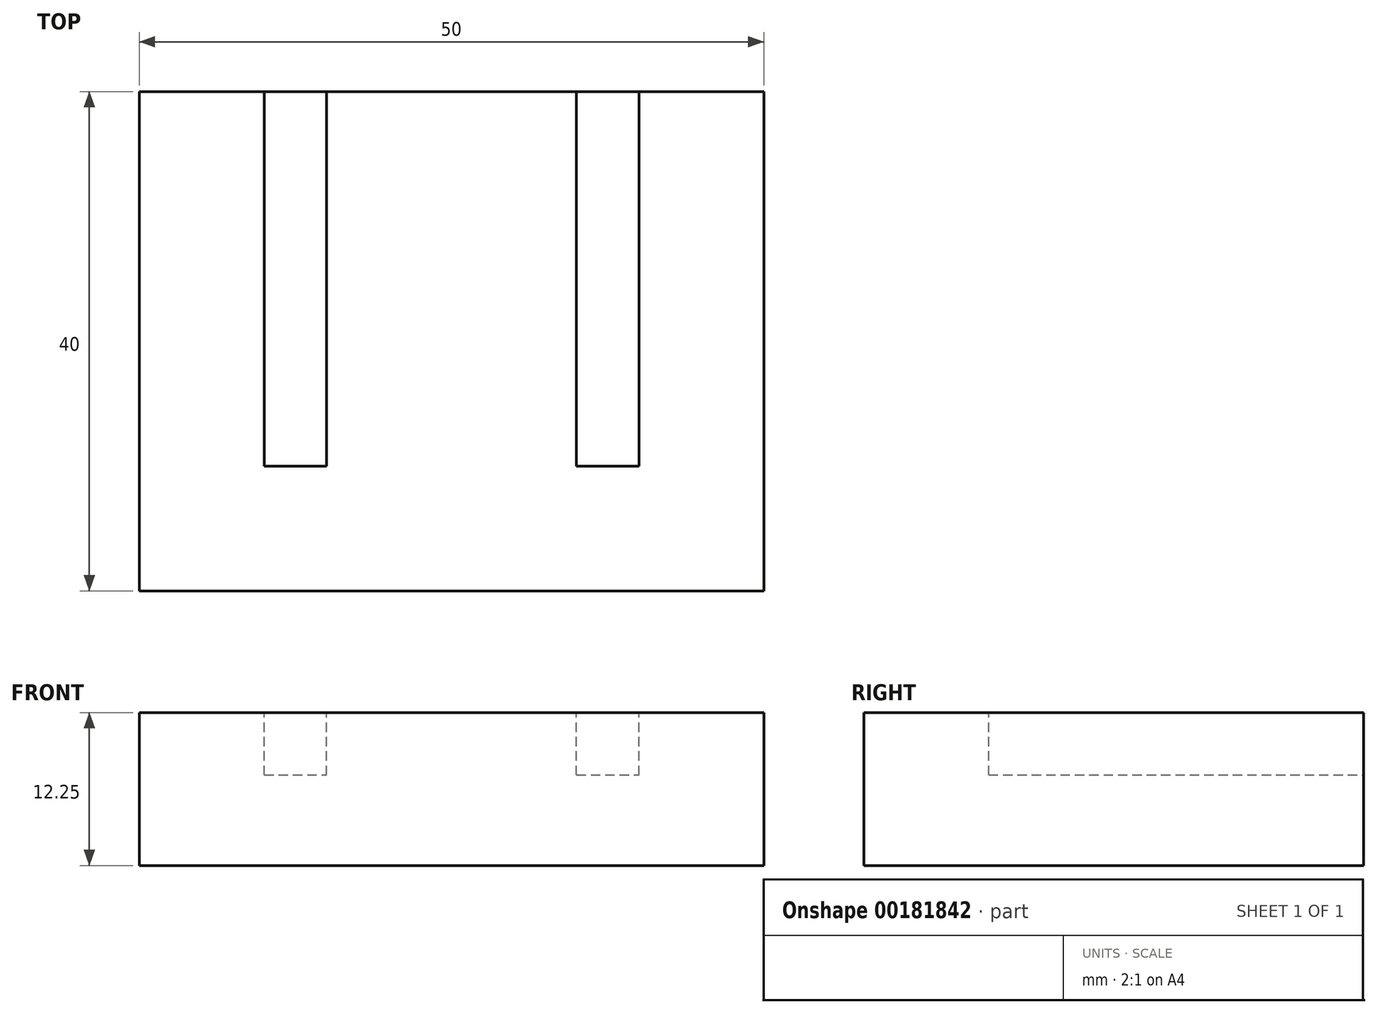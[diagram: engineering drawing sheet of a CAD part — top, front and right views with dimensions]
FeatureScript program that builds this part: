
annotation { "Feature Type Name" : "Feature", "Feature Type Description" : "" }
export const myFeature = defineFeature(function(context is Context, id is Id, definition is map)
    precondition{}
    {
        {
            var Q0;
            Q0=qCreatedBy(makeId("Top.planeOp"),FACE);
            var sketch = newSketch(context, id + "F0", { "sketchPlane" : qUnion([Q0])});
            skLineSegment(sketch, "E0.bottom", {"start": v(-26.25, 21.05) * mm, "end": v(23.75, 21.05) * mm});
            skLineSegment(sketch, "E0.top", {"start": v(-26.25, -18.95) * mm, "end": v(23.75, -18.95) * mm});
            skLineSegment(sketch, "E0.left", {"start": v(-26.25, 21.05) * mm, "end": v(-26.25, -18.95) * mm});
            skLineSegment(sketch, "E0.right", {"start": v(23.75, 21.05) * mm, "end": v(23.75, -18.95) * mm});
            skLineSegment(sketch, "E1", {"start": v(-16.25, 21.05) * mm, "end": v(-16.25, -8.95) * mm});
            skLineSegment(sketch, "E2", {"start": v(-11.25, 21.05) * mm, "end": v(-11.25, -8.95) * mm});
            skLineSegment(sketch, "E3", {"start": v(8.75, -8.95) * mm, "end": v(8.75, 21.05) * mm});
            skLineSegment(sketch, "E4", {"start": v(13.75, 21.05) * mm, "end": v(13.75, -8.95) * mm});
            skLineSegment(sketch, "E5", {"start": v(-26.25, -8.95) * mm, "end": v(23.75, -8.95) * mm});
            skSolve(sketch);
        }
        {
            var Q0;
            Q0 = qSketchRegion(id + "F0", true);
            extrude(context, id + "F1", {"entities" : qUnion([Q0]), "oppositeDirection" : true, "depth" : 12.25 * mm});
        }
        {
            var Q0;
            {var subQ0=sQuery(id+"F0.wireOp",EDGE,"E1");Q0=makeQuery(id+"F0.imprint","IMPRINT",FACE,{"disambiguationData":[TD([[makeQuery(id+"F0.imprint","IMPRINT",EDGE,{"derivedFrom":subQ0}),1.0]])]});}
            var Q1;
            {var subQ0=sQuery(id+"F0.wireOp",EDGE,"E3");Q1=makeQuery(id+"F0.imprint","IMPRINT",FACE,{"disambiguationData":[TD([[makeQuery(id+"F0.imprint","IMPRINT",EDGE,{"derivedFrom":subQ0}),-1.0]])]});}
            extrude(context, id + "F2", {"entities" : qUnion([Q0, Q1]), "operationType" : NewBodyOperationType.REMOVE, "oppositeDirection" : true, "depth" : 5 * mm});
        }
    });
